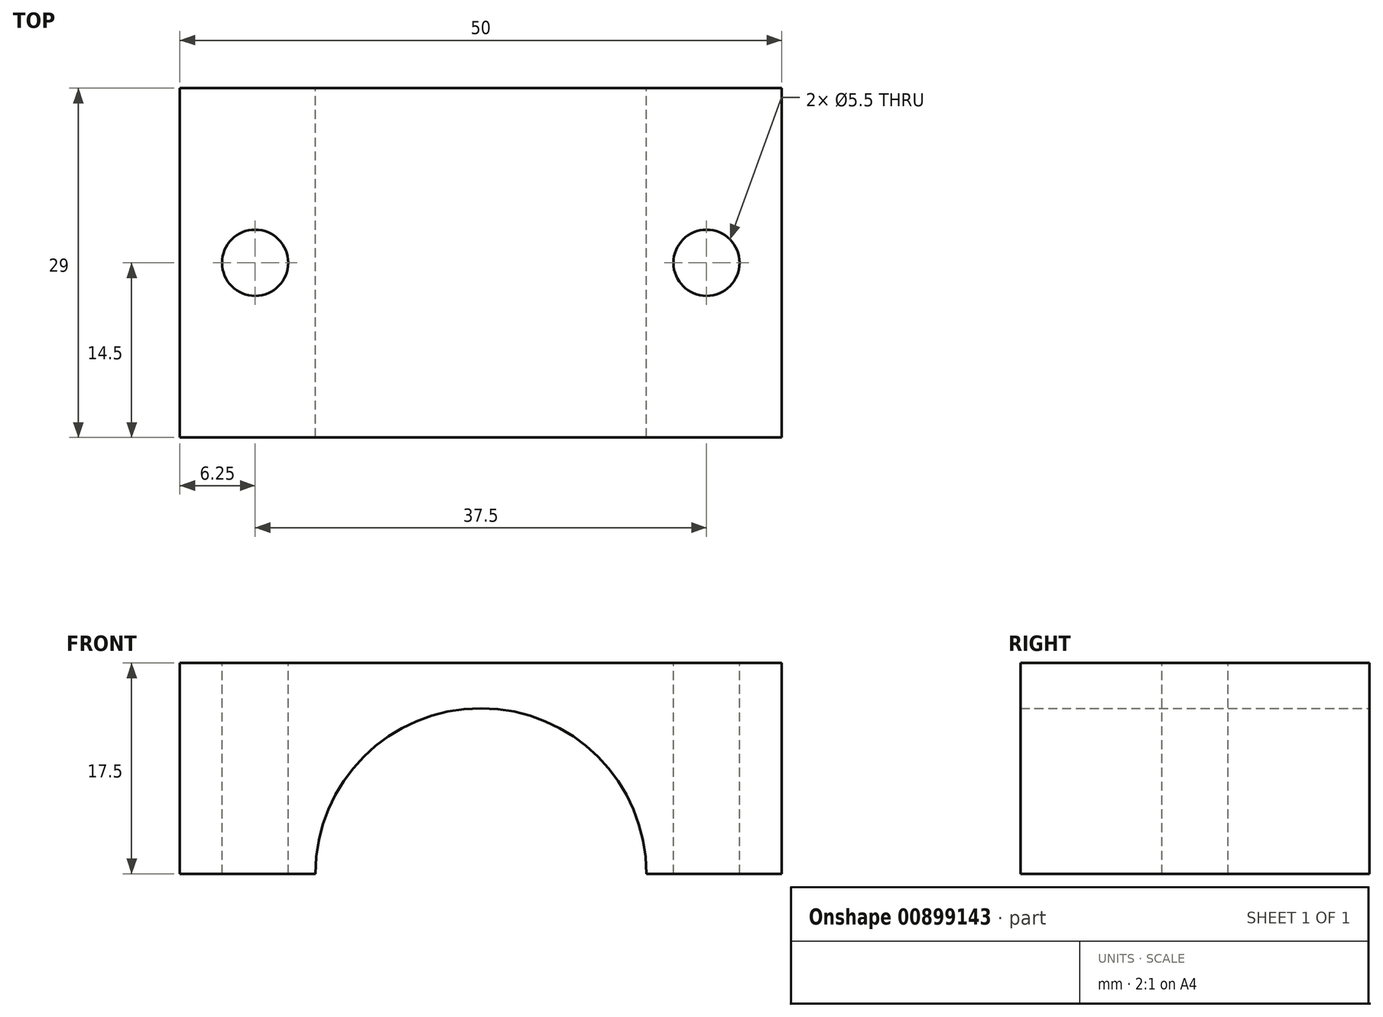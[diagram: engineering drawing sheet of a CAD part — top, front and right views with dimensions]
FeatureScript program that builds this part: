
annotation { "Feature Type Name" : "Feature", "Feature Type Description" : "" }
export const myFeature = defineFeature(function(context is Context, id is Id, definition is map)
    precondition{}
    {
        {
            var Q0;
            Q0=qCreatedBy(makeId("Front.planeOp"),FACE);
            var sketch = newSketch(context, id + "F0", { "sketchPlane" : qUnion([Q0])});
            skArc(sketch, "E0", {"start": v(13.75, 0) * mm, "mid": v(0, 13.75) * mm, "end": v(-13.75, 0) * mm});
            skLineSegment(sketch, "E1", {"start": v(-13.75, 0) * mm, "end": v(-25, 0) * mm});
            skLineSegment(sketch, "E2", {"start": v(-25, 0) * mm, "end": v(-25, 17.5) * mm});
            skLineSegment(sketch, "E3", {"start": v(-25, 17.5) * mm, "end": v(25, 17.5) * mm});
            skLineSegment(sketch, "E4", {"start": v(25, 17.5) * mm, "end": v(25, 0) * mm});
            skLineSegment(sketch, "E5", {"start": v(25, 0) * mm, "end": v(13.75, 0) * mm});
            skSolve(sketch);
        }
        {
            var Q0;
            Q0=qSketchRegion(id+"F0",true);
            extrude(context, id + "F1", {"entities" : qUnion([Q0]), "depth" : 29 * mm, "offsetDistance" : 25 * mm});
        }
        {
            var Q0;
            Q0=makeQuery(id+"F1.opExtrude","SWEPT_FACE",FACE,{"disambiguationData":[OSD([sQuery(id+"F0.wireOp",EDGE,"E3")])]});
            var sketch = newSketch(context, id + "F2", { "sketchPlane" : qUnion([Q0])});
            skCircle(sketch, "E6", {"center": v(-18.75, -14.5) * mm, "radius": 2.75 * mm});
            skPoint(sketch, "E6.centerSnap0", {"position": v(-25, -14.5) * mm});
            skCircle(sketch, "E7", {"center": v(18.75, -14.5) * mm, "radius": 2.75 * mm});
            skPoint(sketch, "E7.centerSnap0", {"position": v(25, -14.5) * mm});
            skSolve(sketch);
        }
        {
            var Q0;
            Q0=qSketchRegion(id+"F2",true);
            extrude(context, id + "F3", {"entities" : qUnion([Q0]), "operationType" : NewBodyOperationType.REMOVE, "oppositeDirection" : true, "depth" : 50 * mm, "offsetDistance" : 25 * mm});
        }
    });
